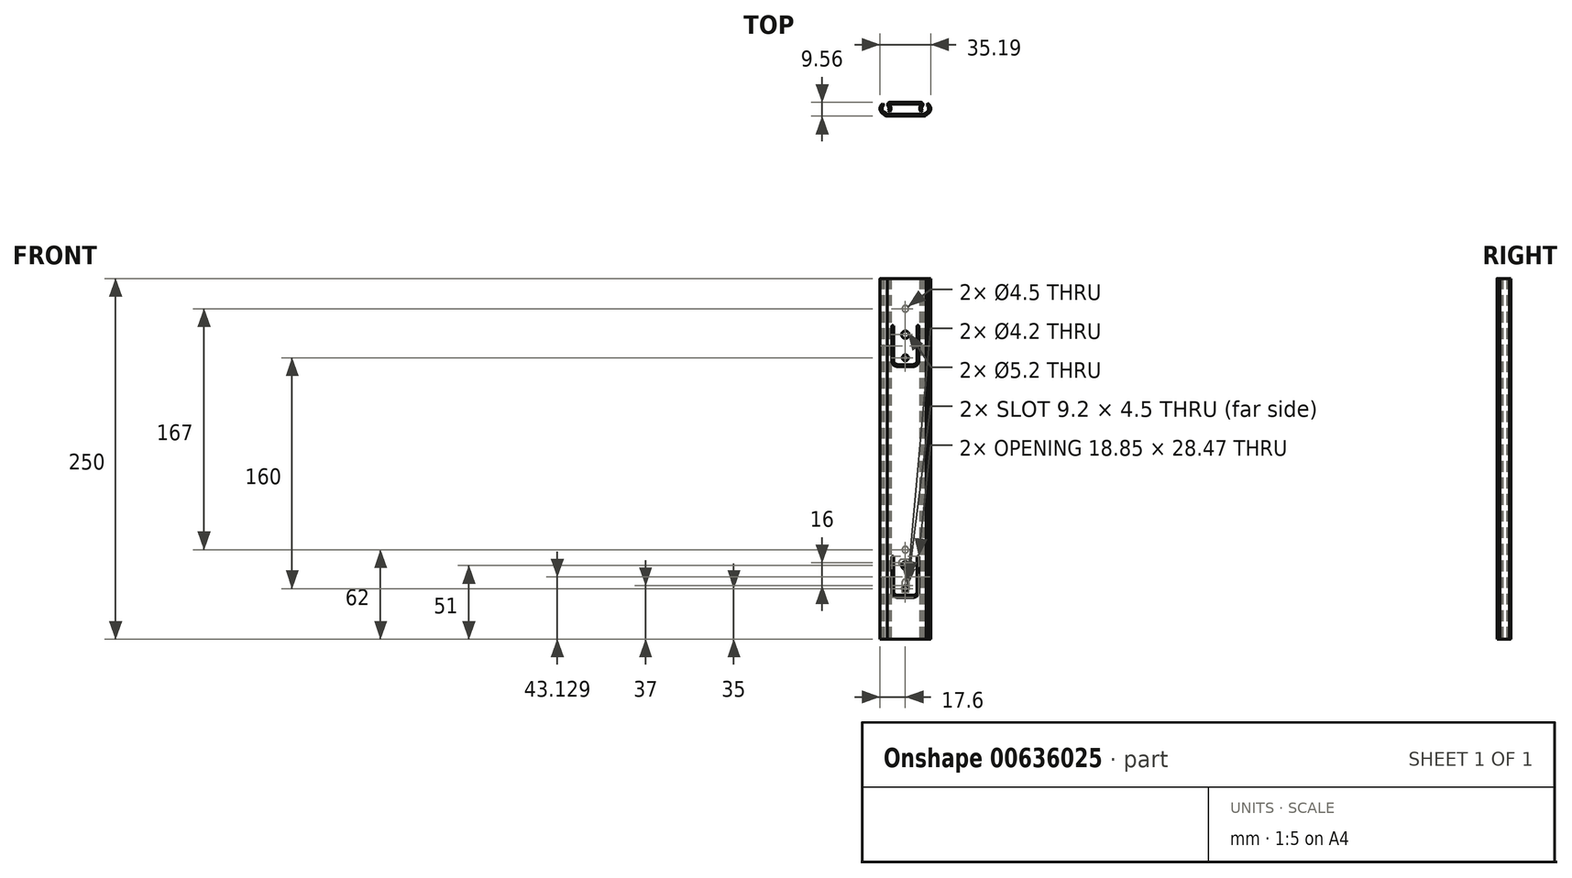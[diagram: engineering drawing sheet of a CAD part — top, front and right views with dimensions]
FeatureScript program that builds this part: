
annotation { "Feature Type Name" : "Feature", "Feature Type Description" : "" }
export const myFeature = defineFeature(function(context is Context, id is Id, definition is map)
    precondition{}
    {
        {
            var Q0;
            Q0=qCreatedBy(makeId("Top.planeOp"),FACE);
            var sketch = newSketch(context, id + "F0", { "sketchPlane" : qUnion([Q0])});
            skLineSegment(sketch, "E0.bottom", {"start": v(-17.6, 4.79) * mm, "end": v(17.6, 4.79) * mm, "construction": true});
            skLineSegment(sketch, "E0.top", {"start": v(-17.6, -4.79) * mm, "end": v(17.6, -4.79) * mm, "construction": true});
            skLineSegment(sketch, "E0.left", {"start": v(-17.6, 4.79) * mm, "end": v(-17.6, -4.79) * mm, "construction": true});
            skLineSegment(sketch, "E0.right", {"start": v(17.6, 4.79) * mm, "end": v(17.6, -4.79) * mm, "construction": true});
            skPoint(sketch, "E0.middle", {"position": v(0, 0) * mm});
            skSolve(sketch);
        }
        {
            var Q0;
            Q0=qCreatedBy(makeId("Top.planeOp"),FACE);
            var sketch = newSketch(context, id + "F1", { "sketchPlane" : qUnion([Q0])});
            skLineSegment(sketch, "E1", {"start": v(-14.63, 2.97) * mm, "end": v(-15.66, 3.97) * mm});
            skArc(sketch, "E2", {"start": v(-15.66, 3.97) * mm, "mid": v(-17.6, 0.62) * mm, "end": v(-16, -2.9) * mm});
            skLineSegment(sketch, "E3", {"start": v(-16, -2.9) * mm, "end": v(-14.51, -4.1) * mm});
            skArc(sketch, "E4", {"start": v(-14.51, -4.1) * mm, "mid": v(-13.6, -4.6) * mm, "end": v(-12.56, -4.76) * mm});
            skLineSegment(sketch, "E5", {"start": v(-12.56, -4.76) * mm, "end": v(12.79, -4.76) * mm});
            skArc(sketch, "E6", {"start": v(12.79, -4.76) * mm, "mid": v(13.6, -4.62) * mm, "end": v(14.32, -4.22) * mm});
            skLineSegment(sketch, "E7", {"start": v(14.32, -4.22) * mm, "end": v(16.16, -2.86) * mm});
            skArc(sketch, "E8", {"start": v(16.16, -2.86) * mm, "mid": v(17.58, 0.66) * mm, "end": v(15.74, 3.98) * mm});
            skLineSegment(sketch, "E9", {"start": v(15.74, 3.98) * mm, "end": v(14.72, 2.95) * mm});
            skArc(sketch, "E10", {"start": v(15.02, -1.9) * mm, "mid": v(16.17, 0.6) * mm, "end": v(14.72, 2.95) * mm});
            skLineSegment(sketch, "E11", {"start": v(15.02, -1.9) * mm, "end": v(13.72, -2.89) * mm});
            skArc(sketch, "E12", {"start": v(12.48, -3.36) * mm, "mid": v(13.13, -3.21) * mm, "end": v(13.72, -2.89) * mm});
            skLineSegment(sketch, "E13", {"start": v(12.48, -3.36) * mm, "end": v(-12.2, -3.36) * mm});
            skArc(sketch, "E14", {"start": v(-13.47, -2.96) * mm, "mid": v(-12.87, -3.25) * mm, "end": v(-12.2, -3.36) * mm});
            skLineSegment(sketch, "E15", {"start": v(-13.47, -2.96) * mm, "end": v(-15.04, -1.87) * mm});
            skArc(sketch, "E16", {"start": v(-14.63, 2.97) * mm, "mid": v(-16.13, 0.66) * mm, "end": v(-15.04, -1.87) * mm});
            skArc(sketch, "E17", {"start": v(-10.73, -1.87) * mm, "mid": v(-9.94, 0.36) * mm, "end": v(-10.58, 2.64) * mm});
            skArc(sketch, "E18", {"start": v(-10.26, 3.4) * mm, "mid": v(-10.67, 3.12) * mm, "end": v(-10.58, 2.64) * mm});
            skLineSegment(sketch, "E19", {"start": v(-10.26, 3.4) * mm, "end": v(10.53, 3.4) * mm});
            skArc(sketch, "E20", {"start": v(10.73, 2.73) * mm, "mid": v(10.87, 3.14) * mm, "end": v(10.53, 3.4) * mm});
            skArc(sketch, "E21", {"start": v(10.73, 2.73) * mm, "mid": v(9.95, 0.46) * mm, "end": v(10.73, -1.82) * mm});
            skLineSegment(sketch, "E22", {"start": v(10.73, -1.82) * mm, "end": v(11.86, -0.86) * mm});
            skArc(sketch, "E23", {"start": v(11.96, 2.13) * mm, "mid": v(11.37, 0.65) * mm, "end": v(11.86, -0.86) * mm});
            skArc(sketch, "E24", {"start": v(11.96, 2.13) * mm, "mid": v(12.15, 2.75) * mm, "end": v(12.16, 3.4) * mm});
            skArc(sketch, "E25", {"start": v(12.16, 3.4) * mm, "mid": v(11.72, 4.4) * mm, "end": v(10.68, 4.8) * mm});
            skLineSegment(sketch, "E26", {"start": v(10.68, 4.8) * mm, "end": v(-10.73, 4.8) * mm});
            skArc(sketch, "E27", {"start": v(-10.73, 4.8) * mm, "mid": v(-11.79, 4.36) * mm, "end": v(-12.21, 3.3) * mm});
            skArc(sketch, "E28", {"start": v(-12.21, 3.3) * mm, "mid": v(-12.15, 2.61) * mm, "end": v(-11.82, 2.02) * mm});
            skArc(sketch, "E29", {"start": v(-11.82, -0.87) * mm, "mid": v(-11.36, 0.57) * mm, "end": v(-11.82, 2.02) * mm});
            skLineSegment(sketch, "E30", {"start": v(-11.82, -0.87) * mm, "end": v(-10.73, -1.87) * mm});
            skSolve(sketch);
        }
        {
            var Q0;
            Q0=makeQuery(id+"F1.imprint","IMPRINT",FACE,{"disambiguationData":[TD([[makeQuery(id+"F1.imprint","IMPRINT",EDGE,{"derivedFrom":sQuery(id+"F1.wireOp",EDGE,"E17")}),1.0]])]});
            extrude(context, id + "F2", {"entities" : qUnion([Q0]), "depth" : 250 * mm, "offsetDistance" : 25 * mm});
        }
        {
            var Q0;
            Q0=makeQuery(id+"F1.imprint","IMPRINT",FACE,{"disambiguationData":[TD([[makeQuery(id+"F1.imprint","IMPRINT",EDGE,{"derivedFrom":sQuery(id+"F1.wireOp",EDGE,"E1")}),1.0]])]});
            extrude(context, id + "F3", {"entities" : qUnion([Q0]), "depth" : 250 * mm, "offsetDistance" : 25 * mm});
        }
        {
            var Q0;
            Q0=makeQuery(id+"F3.opExtrude","SWEPT_FACE",FACE,{"disambiguationData":[OSD([sQuery(id+"F1.wireOp",EDGE,"E5")])]});
            var sketch = newSketch(context, id + "F4", { "sketchPlane" : qUnion([Q0])});
            skLineSegment(sketch, "E31", {"start": v(0, 0) * mm, "end": v(0, 250) * mm, "construction": true});
            skLineSegment(sketch, "E32.bottom", {"start": v(2.25, 41.6) * mm, "end": v(-2.25, 41.6) * mm});
            skLineSegment(sketch, "E32.top", {"start": v(2.25, 32.4) * mm, "end": v(-2.25, 32.4) * mm});
            skLineSegment(sketch, "E32.left", {"start": v(2.25, 41.6) * mm, "end": v(2.25, 32.4) * mm});
            skLineSegment(sketch, "E32.right", {"start": v(-2.25, 41.6) * mm, "end": v(-2.25, 32.4) * mm});
            skPoint(sketch, "E32.middle", {"position": v(0, 37) * mm});
            skLineSegment(sketch, "E33.bottom", {"start": v(4.6, 55.25) * mm, "end": v(-4.6, 55.25) * mm});
            skLineSegment(sketch, "E33.top", {"start": v(4.6, 50.75) * mm, "end": v(-4.6, 50.75) * mm});
            skLineSegment(sketch, "E33.left", {"start": v(4.6, 55.25) * mm, "end": v(4.6, 50.75) * mm});
            skLineSegment(sketch, "E33.right", {"start": v(-4.6, 55.25) * mm, "end": v(-4.6, 50.75) * mm});
            skPoint(sketch, "E33.middle", {"position": v(0, 53) * mm});
            skCircle(sketch, "E34", {"center": v(0, 62) * mm, "radius": 2.25 * mm});
            skCircle(sketch, "E35", {"center": v(0, 229) * mm, "radius": 2.25 * mm});
            skSolve(sketch);
        }
        {
            var Q0;
            Q0=makeQuery(id+"F4.imprint","IMPRINT",FACE,{"disambiguationData":[TD([[makeQuery(id+"F4.imprint","IMPRINT",EDGE,{"derivedFrom":sQuery(id+"F4.wireOp",EDGE,"E32.bottom")}),1.0]])]});
            var Q1;
            Q1=makeQuery(id+"F4.imprint","IMPRINT",FACE,{"disambiguationData":[TD([[makeQuery(id+"F4.imprint","IMPRINT",EDGE,{"derivedFrom":sQuery(id+"F4.wireOp",EDGE,"E33.bottom")}),1.0]])]});
            var Q2;
            Q2=makeQuery(id+"F4.imprint","IMPRINT",FACE,{"disambiguationData":[TD([[makeQuery(id+"F4.imprint","IMPRINT",EDGE,{"derivedFrom":sQuery(id+"F4.wireOp",EDGE,"E34")}),1.0]])]});
            var Q3;
            Q3=makeQuery(id+"F4.imprint","IMPRINT",FACE,{"disambiguationData":[TD([[makeQuery(id+"F4.imprint","IMPRINT",EDGE,{"derivedFrom":sQuery(id+"F4.wireOp",EDGE,"E35")}),1.0]])]});
            extrude(context, id + "F5", {"entities" : qUnion([Q0, Q1, Q2, Q3]), "depth" : 25 * mm, "offsetDistance" : 25 * mm});
        }
        {
            var Q0;
            Q0=makeQuery(id+"F5.opExtrude","SWEPT_BODY",BODY,{"disambiguationData":[OSD([sQuery(id+"F4.wireOp",EDGE,"E35")])]});
            var Q1;
            Q1=makeQuery(id+"F5.opExtrude","SWEPT_BODY",BODY,{"disambiguationData":[OSD([sQuery(id+"F4.wireOp",EDGE,"E34")])]});
            var Q2;
            Q2=makeQuery(id+"F5.opExtrude","SWEPT_BODY",BODY,{"disambiguationData":[OSD([sQuery(id+"F4.wireOp",EDGE,"E33.bottom"),sQuery(id+"F4.wireOp",EDGE,"E33.top"),sQuery(id+"F4.wireOp",EDGE,"E33.left"),sQuery(id+"F4.wireOp",EDGE,"E33.right")])]});
            var Q3;
            Q3=makeQuery(id+"F5.opExtrude","SWEPT_BODY",BODY,{"disambiguationData":[OSD([sQuery(id+"F4.wireOp",EDGE,"E32.bottom"),sQuery(id+"F4.wireOp",EDGE,"E32.top"),sQuery(id+"F4.wireOp",EDGE,"E32.left"),sQuery(id+"F4.wireOp",EDGE,"E32.right")])]});
            transform(context, id + "F6", {"entities" : qUnion([Q0, Q1, Q2, Q3]), "transformType" : TransformType.TRANSLATION_3D, "dx" : 0 * mm, "dy" : 29 * mm, "dz" : 0 * mm, "makeCopy" : false});
        }
        {
            var Q0;
            Q0=makeQuery(id+"F5.opExtrude","SWEPT_BODY",BODY,{"disambiguationData":[OSD([sQuery(id+"F4.wireOp",EDGE,"E35")])]});
            var Q1;
            Q1=makeQuery(id+"F5.opExtrude","SWEPT_BODY",BODY,{"disambiguationData":[OSD([sQuery(id+"F4.wireOp",EDGE,"E34")])]});
            var Q2;
            Q2=makeQuery(id+"F5.opExtrude","SWEPT_BODY",BODY,{"disambiguationData":[OSD([sQuery(id+"F4.wireOp",EDGE,"E33.bottom"),sQuery(id+"F4.wireOp",EDGE,"E33.top"),sQuery(id+"F4.wireOp",EDGE,"E33.left"),sQuery(id+"F4.wireOp",EDGE,"E33.right")])]});
            var Q3;
            Q3=makeQuery(id+"F5.opExtrude","SWEPT_BODY",BODY,{"disambiguationData":[OSD([sQuery(id+"F4.wireOp",EDGE,"E32.bottom"),sQuery(id+"F4.wireOp",EDGE,"E32.top"),sQuery(id+"F4.wireOp",EDGE,"E32.left"),sQuery(id+"F4.wireOp",EDGE,"E32.right")])]});
            transform(context, id + "F7", {"entities" : qUnion([Q0, Q1, Q2, Q3]), "transformType" : TransformType.TRANSLATION_3D, "dx" : 0 * mm, "dy" : 2.4 * mm, "dz" : 0 * mm, "makeCopy" : false});
        }
        {
            var Q0;
            Q0=makeQuery(id+"F5.opExtrude","SWEPT_EDGE",EDGE,{"disambiguationData":[OSD([sQuery(id+"F4.wireOp",EDGE,"E33.top"),sQuery(id+"F4.wireOp",EDGE,"E33.right")])]});
            var Q1;
            Q1=makeQuery(id+"F5.opExtrude","SWEPT_EDGE",EDGE,{"disambiguationData":[OSD([sQuery(id+"F4.wireOp",EDGE,"E33.top"),sQuery(id+"F4.wireOp",EDGE,"E33.left")])]});
            var Q2;
            Q2=makeQuery(id+"F5.opExtrude","SWEPT_EDGE",EDGE,{"disambiguationData":[OSD([sQuery(id+"F4.wireOp",EDGE,"E32.bottom"),sQuery(id+"F4.wireOp",EDGE,"E32.right")])]});
            var Q3;
            Q3=makeQuery(id+"F5.opExtrude","SWEPT_EDGE",EDGE,{"disambiguationData":[OSD([sQuery(id+"F4.wireOp",EDGE,"E32.top"),sQuery(id+"F4.wireOp",EDGE,"E32.right")])]});
            var Q4;
            Q4=makeQuery(id+"F5.opExtrude","SWEPT_EDGE",EDGE,{"disambiguationData":[OSD([sQuery(id+"F4.wireOp",EDGE,"E32.top"),sQuery(id+"F4.wireOp",EDGE,"E32.left")])]});
            var Q5;
            Q5=makeQuery(id+"F5.opExtrude","SWEPT_EDGE",EDGE,{"disambiguationData":[OSD([sQuery(id+"F4.wireOp",EDGE,"E33.bottom"),sQuery(id+"F4.wireOp",EDGE,"E33.right")])]});
            var Q6;
            Q6=makeQuery(id+"F5.opExtrude","SWEPT_EDGE",EDGE,{"disambiguationData":[OSD([sQuery(id+"F4.wireOp",EDGE,"E33.bottom"),sQuery(id+"F4.wireOp",EDGE,"E33.left")])]});
            var Q7;
            Q7=makeQuery(id+"F5.opExtrude","SWEPT_EDGE",EDGE,{"disambiguationData":[OSD([sQuery(id+"F4.wireOp",EDGE,"E32.bottom"),sQuery(id+"F4.wireOp",EDGE,"E32.left")])]});
            fillet(context, id + "F8", {"entities" : qUnion([Q0, Q1, Q2, Q3, Q4, Q5, Q6, Q7]), "radius" : 2.25 * mm, "tangentPropagation" : true, "allowEdgeOverflow" : false});
        }
        {
            var Q0;
            Q0=makeQuery(id+"F5.opExtrude","SWEPT_BODY",BODY,{"disambiguationData":[OSD([sQuery(id+"F4.wireOp",EDGE,"E32.bottom"),sQuery(id+"F4.wireOp",EDGE,"E32.top"),sQuery(id+"F4.wireOp",EDGE,"E32.left"),sQuery(id+"F4.wireOp",EDGE,"E32.right")])]});
            var Q1;
            Q1=makeQuery(id+"F2.opExtrude","SWEPT_BODY",BODY,{"disambiguationData":[OSD([sQuery(id+"F1.wireOp",EDGE,"E17"),sQuery(id+"F1.wireOp",EDGE,"E18"),sQuery(id+"F1.wireOp",EDGE,"E19"),sQuery(id+"F1.wireOp",EDGE,"E20"),sQuery(id+"F1.wireOp",EDGE,"E21"),sQuery(id+"F1.wireOp",EDGE,"E22"),sQuery(id+"F1.wireOp",EDGE,"E23"),sQuery(id+"F1.wireOp",EDGE,"E24"),sQuery(id+"F1.wireOp",EDGE,"E25"),sQuery(id+"F1.wireOp",EDGE,"E26"),sQuery(id+"F1.wireOp",EDGE,"E27"),sQuery(id+"F1.wireOp",EDGE,"E28"),sQuery(id+"F1.wireOp",EDGE,"E29"),sQuery(id+"F1.wireOp",EDGE,"E30")])]});
            booleanBodies(context, id + "F9", {"operationType" : BooleanOperationType.SUBTRACTION, "tools" : qUnion([Q0]), "targets" : qUnion([Q1])});
        }
        {
            var Q0;
            Q0=makeQuery(id+"F5.opExtrude","SWEPT_BODY",BODY,{"disambiguationData":[OSD([sQuery(id+"F4.wireOp",EDGE,"E35")])]});
            var Q1;
            Q1=makeQuery(id+"F2.opExtrude","SWEPT_BODY",BODY,{"disambiguationData":[OSD([sQuery(id+"F1.wireOp",EDGE,"E17"),sQuery(id+"F1.wireOp",EDGE,"E18"),sQuery(id+"F1.wireOp",EDGE,"E19"),sQuery(id+"F1.wireOp",EDGE,"E20"),sQuery(id+"F1.wireOp",EDGE,"E21"),sQuery(id+"F1.wireOp",EDGE,"E22"),sQuery(id+"F1.wireOp",EDGE,"E23"),sQuery(id+"F1.wireOp",EDGE,"E24"),sQuery(id+"F1.wireOp",EDGE,"E25"),sQuery(id+"F1.wireOp",EDGE,"E26"),sQuery(id+"F1.wireOp",EDGE,"E27"),sQuery(id+"F1.wireOp",EDGE,"E28"),sQuery(id+"F1.wireOp",EDGE,"E29"),sQuery(id+"F1.wireOp",EDGE,"E30")])]});
            booleanBodies(context, id + "F10", {"operationType" : BooleanOperationType.SUBTRACTION, "tools" : qUnion([Q0]), "targets" : qUnion([Q1])});
        }
        {
            var Q0;
            Q0=makeQuery(id+"F5.opExtrude","SWEPT_BODY",BODY,{"disambiguationData":[OSD([sQuery(id+"F4.wireOp",EDGE,"E33.bottom"),sQuery(id+"F4.wireOp",EDGE,"E33.top"),sQuery(id+"F4.wireOp",EDGE,"E33.left"),sQuery(id+"F4.wireOp",EDGE,"E33.right")])]});
            var Q1;
            Q1=makeQuery(id+"F2.opExtrude","SWEPT_BODY",BODY,{"disambiguationData":[OSD([sQuery(id+"F1.wireOp",EDGE,"E17"),sQuery(id+"F1.wireOp",EDGE,"E18"),sQuery(id+"F1.wireOp",EDGE,"E19"),sQuery(id+"F1.wireOp",EDGE,"E20"),sQuery(id+"F1.wireOp",EDGE,"E21"),sQuery(id+"F1.wireOp",EDGE,"E22"),sQuery(id+"F1.wireOp",EDGE,"E23"),sQuery(id+"F1.wireOp",EDGE,"E24"),sQuery(id+"F1.wireOp",EDGE,"E25"),sQuery(id+"F1.wireOp",EDGE,"E26"),sQuery(id+"F1.wireOp",EDGE,"E27"),sQuery(id+"F1.wireOp",EDGE,"E28"),sQuery(id+"F1.wireOp",EDGE,"E29"),sQuery(id+"F1.wireOp",EDGE,"E30")])]});
            booleanBodies(context, id + "F11", {"operationType" : BooleanOperationType.SUBTRACTION, "tools" : qUnion([Q0]), "targets" : qUnion([Q1])});
        }
        {
            var Q0;
            Q0=makeQuery(id+"F5.opExtrude","SWEPT_BODY",BODY,{"disambiguationData":[OSD([sQuery(id+"F4.wireOp",EDGE,"E34")])]});
            var Q1;
            Q1=makeQuery(id+"F2.opExtrude","SWEPT_BODY",BODY,{"disambiguationData":[OSD([sQuery(id+"F1.wireOp",EDGE,"E17"),sQuery(id+"F1.wireOp",EDGE,"E18"),sQuery(id+"F1.wireOp",EDGE,"E19"),sQuery(id+"F1.wireOp",EDGE,"E20"),sQuery(id+"F1.wireOp",EDGE,"E21"),sQuery(id+"F1.wireOp",EDGE,"E22"),sQuery(id+"F1.wireOp",EDGE,"E23"),sQuery(id+"F1.wireOp",EDGE,"E24"),sQuery(id+"F1.wireOp",EDGE,"E25"),sQuery(id+"F1.wireOp",EDGE,"E26"),sQuery(id+"F1.wireOp",EDGE,"E27"),sQuery(id+"F1.wireOp",EDGE,"E28"),sQuery(id+"F1.wireOp",EDGE,"E29"),sQuery(id+"F1.wireOp",EDGE,"E30")])]});
            booleanBodies(context, id + "F12", {"operationType" : BooleanOperationType.SUBTRACTION, "tools" : qUnion([Q0]), "targets" : qUnion([Q1])});
        }
        {
            var Q0;
            Q0=qCreatedBy(makeId("Front.planeOp"),FACE);
            var sketch = newSketch(context, id + "F13", { "sketchPlane" : qUnion([Q0])});
            skLineSegment(sketch, "E36", {"start": v(0, 306.25) * mm, "end": v(0, 0) * mm, "construction": true});
            skCircle(sketch, "E37", {"center": v(0, 35) * mm, "radius": 2.1 * mm});
            skCircle(sketch, "E38", {"center": v(0, 51) * mm, "radius": 2.6 * mm});
            skLineSegment(sketch, "E39", {"start": v(0, 28.9) * mm, "end": v(-9.42, 28.9) * mm});
            skLineSegment(sketch, "E40", {"start": v(-9.42, 28.9) * mm, "end": v(-9.42, 57.36) * mm});
            skLineSegment(sketch, "E41", {"start": v(-9.42, 57.36) * mm, "end": v(-8.13, 57.36) * mm});
            skLineSegment(sketch, "E42", {"start": v(-8.13, 57.36) * mm, "end": v(-8.13, 30.3) * mm});
            skLineSegment(sketch, "E43", {"start": v(-8.13, 30.3) * mm, "end": v(0, 30.3) * mm});
            skLineSegment(sketch, "E44", {"start": v(0, 30.3) * mm, "end": v(0, 28.9) * mm});
            skLineSegment(sketch, "E45.MirrorCS", {"start": v(9.42, 57.36) * mm, "end": v(8.13, 57.36) * mm});
            skLineSegment(sketch, "E46.MirrorCS", {"start": v(9.42, 28.9) * mm, "end": v(9.42, 57.36) * mm});
            skLineSegment(sketch, "E47.MirrorCS", {"start": v(8.13, 57.36) * mm, "end": v(8.13, 30.3) * mm});
            skLineSegment(sketch, "E48.MirrorCS", {"start": v(0, 28.9) * mm, "end": v(9.42, 28.9) * mm});
            skLineSegment(sketch, "E49.MirrorCS", {"start": v(8.13, 30.3) * mm, "end": v(0, 30.3) * mm});
            skPoint(sketch, "E50", {"position": v(0, 195) * mm});
            skLineSegment(sketch, "E51", {"start": v(0.05, 195) * mm, "end": v(-0.05, 195) * mm, "construction": true});
            skLineSegment(sketch, "E52", {"start": v(0, 195.05) * mm, "end": v(0, 194.95) * mm});
            skSolve(sketch);
        }
        {
            var Q0;
            Q0=makeQuery(id+"F13.imprint","IMPRINT",FACE,{"disambiguationData":[TD([[makeQuery(id+"F13.imprint","IMPRINT",EDGE,{"derivedFrom":sQuery(id+"F13.wireOp",EDGE,"E39")}),-1.0]])]});
            var Q1;
            Q1=makeQuery(id+"F13.imprint","IMPRINT",FACE,{"disambiguationData":[TD([[makeQuery(id+"F13.imprint","IMPRINT",EDGE,{"derivedFrom":sQuery(id+"F13.wireOp",EDGE,"E44")}),1.0]])]});
            var Q2;
            Q2=makeQuery(id+"F13.imprint","IMPRINT",FACE,{"disambiguationData":[TD([[makeQuery(id+"F13.imprint","IMPRINT",EDGE,{"derivedFrom":sQuery(id+"F13.wireOp",EDGE,"E37")}),1.0]])]});
            var Q3;
            Q3=makeQuery(id+"F13.imprint","IMPRINT",FACE,{"disambiguationData":[TD([[makeQuery(id+"F13.imprint","IMPRINT",EDGE,{"derivedFrom":sQuery(id+"F13.wireOp",EDGE,"E38")}),1.0]])]});
            extrude(context, id + "F14", {"entities" : qUnion([Q0, Q1, Q2, Q3]), "depth" : 6 * mm, "offsetDistance" : 25 * mm});
        }
        {
            var Q0;
            Q0=makeQuery(id+"F14.opExtrude","SWEPT_EDGE",EDGE,{"disambiguationData":[OSD([sQuery(id+"F13.wireOp",EDGE,"E46.MirrorCS"),sQuery(id+"F13.wireOp",EDGE,"E48.MirrorCS")])]});
            var Q1;
            Q1=makeQuery(id+"F14.opExtrude","SWEPT_EDGE",EDGE,{"disambiguationData":[OSD([sQuery(id+"F13.wireOp",EDGE,"E39"),sQuery(id+"F13.wireOp",EDGE,"E40")])]});
            fillet(context, id + "F15", {"entities" : qUnion([Q0, Q1]), "radius" : 4 * mm, "tangentPropagation" : true, "allowEdgeOverflow" : false});
        }
        {
            var Q0;
            Q0=makeQuery(id+"F14.opExtrude","SWEPT_EDGE",EDGE,{"disambiguationData":[OSD([sQuery(id+"F13.wireOp",EDGE,"E42"),sQuery(id+"F13.wireOp",EDGE,"E43")])]});
            var Q1;
            Q1=makeQuery(id+"F14.opExtrude","SWEPT_EDGE",EDGE,{"disambiguationData":[OSD([sQuery(id+"F13.wireOp",EDGE,"E47.MirrorCS"),sQuery(id+"F13.wireOp",EDGE,"E49.MirrorCS")])]});
            fillet(context, id + "F16", {"entities" : qUnion([Q0, Q1]), "radius" : 2.8 * mm, "tangentPropagation" : true, "allowEdgeOverflow" : false});
        }
        {
            var Q0;
            Q0=makeQuery(id+"F14.opExtrude","SWEPT_EDGE",EDGE,{"disambiguationData":[OSD([sQuery(id+"F13.wireOp",EDGE,"E41"),sQuery(id+"F13.wireOp",EDGE,"E42")])]});
            var Q1;
            Q1=makeQuery(id+"F14.opExtrude","SWEPT_EDGE",EDGE,{"disambiguationData":[OSD([sQuery(id+"F13.wireOp",EDGE,"E40"),sQuery(id+"F13.wireOp",EDGE,"E41")])]});
            var Q2;
            Q2=makeQuery(id+"F14.opExtrude","SWEPT_EDGE",EDGE,{"disambiguationData":[OSD([sQuery(id+"F13.wireOp",EDGE,"E45.MirrorCS"),sQuery(id+"F13.wireOp",EDGE,"E47.MirrorCS")])]});
            var Q3;
            Q3=makeQuery(id+"F14.opExtrude","SWEPT_EDGE",EDGE,{"disambiguationData":[OSD([sQuery(id+"F13.wireOp",EDGE,"E45.MirrorCS"),sQuery(id+"F13.wireOp",EDGE,"E46.MirrorCS")])]});
            fillet(context, id + "F17", {"entities" : qUnion([Q0, Q1, Q2, Q3]), "radius" : .7 * mm, "tangentPropagation" : true, "allowEdgeOverflow" : false});
        }
        {
            var Q0;
            Q0=makeQuery(id+"F14.opExtrude","SWEPT_BODY",BODY,{"disambiguationData":[OSD([sQuery(id+"F13.wireOp",EDGE,"E37")])]});
            var Q1;
            Q1=makeQuery(id+"F14.opExtrude","SWEPT_BODY",BODY,{"disambiguationData":[OSD([sQuery(id+"F13.wireOp",EDGE,"E38")])]});
            var Q2;
            Q2=makeQuery(id+"F14.opExtrude","SWEPT_BODY",BODY,{"disambiguationData":[OSD([sQuery(id+"F13.wireOp",EDGE,"E39"),sQuery(id+"F13.wireOp",EDGE,"E40"),sQuery(id+"F13.wireOp",EDGE,"E41"),sQuery(id+"F13.wireOp",EDGE,"E42"),sQuery(id+"F13.wireOp",EDGE,"E43"),sQuery(id+"F13.wireOp",EDGE,"E45.MirrorCS"),sQuery(id+"F13.wireOp",EDGE,"E46.MirrorCS"),sQuery(id+"F13.wireOp",EDGE,"E47.MirrorCS"),sQuery(id+"F13.wireOp",EDGE,"E48.MirrorCS"),sQuery(id+"F13.wireOp",EDGE,"E49.MirrorCS")])]});
            transform(context, id + "F18", {"entities" : qUnion([Q0, Q1, Q2]), "transformType" : TransformType.TRANSLATION_3D, "dx" : 0 * mm, "dy" : 0 * mm, "dz" : 97 * mm, "makeCopy" : true});
        }
        {
            var Q0;
            Q0=makeQuery(id+"F18.opPattern","COPY",BODY,{"derivedFrom":makeQuery(id+"F14.opExtrude","SWEPT_BODY",BODY,{"disambiguationData":[OSD([sQuery(id+"F13.wireOp",EDGE,"E38")])]}),"instanceName":"1"});
            var Q1;
            Q1=makeQuery(id+"F18.opPattern","COPY",BODY,{"derivedFrom":makeQuery(id+"F14.opExtrude","SWEPT_BODY",BODY,{"disambiguationData":[OSD([sQuery(id+"F13.wireOp",EDGE,"E37")])]}),"instanceName":"1"});
            var Q2;
            Q2=makeQuery(id+"F18.opPattern","COPY",BODY,{"derivedFrom":makeQuery(id+"F14.opExtrude","SWEPT_BODY",BODY,{"disambiguationData":[OSD([sQuery(id+"F13.wireOp",EDGE,"E39"),sQuery(id+"F13.wireOp",EDGE,"E40"),sQuery(id+"F13.wireOp",EDGE,"E41"),sQuery(id+"F13.wireOp",EDGE,"E42"),sQuery(id+"F13.wireOp",EDGE,"E43"),sQuery(id+"F13.wireOp",EDGE,"E45.MirrorCS"),sQuery(id+"F13.wireOp",EDGE,"E46.MirrorCS"),sQuery(id+"F13.wireOp",EDGE,"E47.MirrorCS"),sQuery(id+"F13.wireOp",EDGE,"E48.MirrorCS"),sQuery(id+"F13.wireOp",EDGE,"E49.MirrorCS")])]}),"instanceName":"1"});
            var Q3;
            Q3=makeQuery(id+"F18.opPattern","COPY",EDGE,{"derivedFrom":makeQuery(id+"F14.opExtrude","CAP_EDGE",EDGE,{"disambiguationData":[OSD([sQuery(id+"F13.wireOp",EDGE,"E46.MirrorCS")])],"isStart":false}),"instanceName":"1"});
            transform(context, id + "F19", {"entities" : qUnion([Q0, Q1, Q2]), "transformType" : TransformType.TRANSLATION_DISTANCE, "transformDirection" : qUnion([Q3]), "distance" : 63 * mm, "makeCopy" : false});
        }
        {
            var Q0;
            Q0=makeQuery(id+"F18.opPattern","COPY",BODY,{"derivedFrom":makeQuery(id+"F14.opExtrude","SWEPT_BODY",BODY,{"disambiguationData":[OSD([sQuery(id+"F13.wireOp",EDGE,"E37")])]}),"instanceName":"1"});
            var Q1;
            Q1=makeQuery(id+"F14.opExtrude","SWEPT_BODY",BODY,{"disambiguationData":[OSD([sQuery(id+"F13.wireOp",EDGE,"E39"),sQuery(id+"F13.wireOp",EDGE,"E40"),sQuery(id+"F13.wireOp",EDGE,"E41"),sQuery(id+"F13.wireOp",EDGE,"E42"),sQuery(id+"F13.wireOp",EDGE,"E43"),sQuery(id+"F13.wireOp",EDGE,"E45.MirrorCS"),sQuery(id+"F13.wireOp",EDGE,"E46.MirrorCS"),sQuery(id+"F13.wireOp",EDGE,"E47.MirrorCS"),sQuery(id+"F13.wireOp",EDGE,"E48.MirrorCS"),sQuery(id+"F13.wireOp",EDGE,"E49.MirrorCS")])]});
            var Q2;
            Q2=makeQuery(id+"F14.opExtrude","SWEPT_BODY",BODY,{"disambiguationData":[OSD([sQuery(id+"F13.wireOp",EDGE,"E38")])]});
            var Q3;
            Q3=makeQuery(id+"F18.opPattern","COPY",BODY,{"derivedFrom":makeQuery(id+"F14.opExtrude","SWEPT_BODY",BODY,{"disambiguationData":[OSD([sQuery(id+"F13.wireOp",EDGE,"E38")])]}),"instanceName":"1"});
            var Q4;
            Q4=makeQuery(id+"F18.opPattern","COPY",BODY,{"derivedFrom":makeQuery(id+"F14.opExtrude","SWEPT_BODY",BODY,{"disambiguationData":[OSD([sQuery(id+"F13.wireOp",EDGE,"E39"),sQuery(id+"F13.wireOp",EDGE,"E40"),sQuery(id+"F13.wireOp",EDGE,"E41"),sQuery(id+"F13.wireOp",EDGE,"E42"),sQuery(id+"F13.wireOp",EDGE,"E43"),sQuery(id+"F13.wireOp",EDGE,"E45.MirrorCS"),sQuery(id+"F13.wireOp",EDGE,"E46.MirrorCS"),sQuery(id+"F13.wireOp",EDGE,"E47.MirrorCS"),sQuery(id+"F13.wireOp",EDGE,"E48.MirrorCS"),sQuery(id+"F13.wireOp",EDGE,"E49.MirrorCS")])]}),"instanceName":"1"});
            var Q5;
            Q5=makeQuery(id+"F14.opExtrude","SWEPT_BODY",BODY,{"disambiguationData":[OSD([sQuery(id+"F13.wireOp",EDGE,"E37")])]});
            var Q6;
            Q6=makeQuery(id+"F3.opExtrude","SWEPT_BODY",BODY,{"disambiguationData":[OSD([sQuery(id+"F1.wireOp",EDGE,"E1"),sQuery(id+"F1.wireOp",EDGE,"E2"),sQuery(id+"F1.wireOp",EDGE,"E3"),sQuery(id+"F1.wireOp",EDGE,"E4"),sQuery(id+"F1.wireOp",EDGE,"E5"),sQuery(id+"F1.wireOp",EDGE,"E6"),sQuery(id+"F1.wireOp",EDGE,"E7"),sQuery(id+"F1.wireOp",EDGE,"E8"),sQuery(id+"F1.wireOp",EDGE,"E9"),sQuery(id+"F1.wireOp",EDGE,"E10"),sQuery(id+"F1.wireOp",EDGE,"E11"),sQuery(id+"F1.wireOp",EDGE,"E12"),sQuery(id+"F1.wireOp",EDGE,"E13"),sQuery(id+"F1.wireOp",EDGE,"E14"),sQuery(id+"F1.wireOp",EDGE,"E15"),sQuery(id+"F1.wireOp",EDGE,"E16")])]});
            booleanBodies(context, id + "F20", {"operationType" : BooleanOperationType.SUBTRACTION, "tools" : qUnion([Q0, Q1, Q2, Q3, Q4, Q5]), "targets" : qUnion([Q6])});
        }
    });
